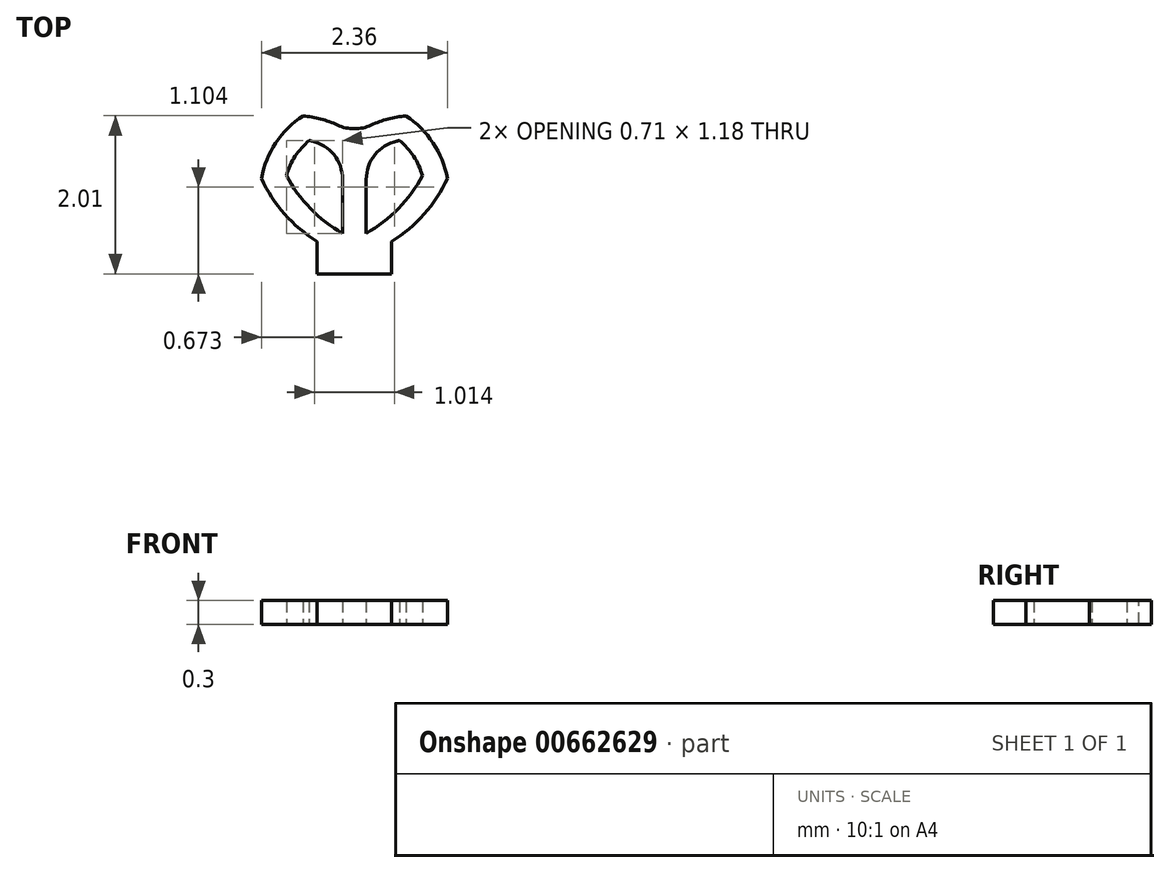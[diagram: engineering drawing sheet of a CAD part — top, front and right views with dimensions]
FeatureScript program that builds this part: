
annotation { "Feature Type Name" : "Feature", "Feature Type Description" : "" }
export const myFeature = defineFeature(function(context is Context, id is Id, definition is map)
    precondition{}
    {
        {
            var Q0;
            Q0=qCreatedBy(makeId("Top.planeOp"),FACE);
            var sketch = newSketch(context, id + "F0", { "sketchPlane" : qUnion([Q0])});
            skArc(sketch, "E0", {"start": v(-0.65, 1) * mm, "mid": v(-1, 0.67) * mm, "end": v(-1.18, 0.21) * mm});
            skLineSegment(sketch, "E1", {"start": v(0, -1) * mm, "end": v(-0.47, -1) * mm});
            skLineSegment(sketch, "E2", {"start": v(-0.47, -1) * mm, "end": v(-0.47, -0.59) * mm});
            skArc(sketch, "E3", {"start": v(0, 0.76) * mm, "mid": v(-0.3, 0.93) * mm, "end": v(-0.65, 1) * mm});
            skArc(sketch, "E4.0", {"start": v(-0.54, 0.69) * mm, "mid": v(-0.56, 0.7) * mm, "end": v(-0.57, 0.7) * mm});
            skArc(sketch, "E5", {"start": v(-0.57, 0.7) * mm, "mid": v(-0.75, 0.5) * mm, "end": v(-0.86, 0.25) * mm});
            skLineSegment(sketch, "E6.0", {"start": v(-0.15, 0.2) * mm, "end": v(-0.15, -0.49) * mm});
            skArc(sketch, "E7", {"start": v(-0.86, 0.25) * mm, "mid": v(-0.56, -0.17) * mm, "end": v(-0.15, -0.49) * mm});
            skArc(sketch, "E8.trimOffspring", {"start": v(-1.18, 0.21) * mm, "mid": v(-0.89, -0.24) * mm, "end": v(-0.47, -0.59) * mm});
            skPoint(sketch, "E9.orphan", {"position": v(-0.47, -0.68) * mm});
            skPoint(sketch, "E10.visualSharp", {"position": v(-0.15, 0.2) * mm});
            skArc(sketch, "E10.filletArc", {"start": v(-0.15, 0.2) * mm, "mid": v(-0.26, 0.51) * mm, "end": v(-0.54, 0.69) * mm});
            skArc(sketch, "E11.MirrorCS", {"start": v(0.54, 0.69) * mm, "mid": v(0.56, 0.7) * mm, "end": v(0.57, 0.7) * mm});
            skLineSegment(sketch, "E12.MirrorCS", {"start": v(0, -1) * mm, "end": v(0.47, -1) * mm});
            skArc(sketch, "E13.MirrorCS", {"start": v(0.65, 1) * mm, "mid": v(1, 0.67) * mm, "end": v(1.18, 0.21) * mm});
            skPoint(sketch, "E14.MirrorP", {"position": v(0.15, 0.2) * mm});
            skArc(sketch, "E15.MirrorCS", {"start": v(0, 0.76) * mm, "mid": v(0.3, 0.93) * mm, "end": v(0.65, 1) * mm});
            skArc(sketch, "E16.MirrorCS", {"start": v(0.57, 0.7) * mm, "mid": v(0.75, 0.5) * mm, "end": v(0.86, 0.25) * mm});
            skArc(sketch, "E17.MirrorCS", {"start": v(1.18, 0.21) * mm, "mid": v(0.89, -0.24) * mm, "end": v(0.47, -0.59) * mm});
            skPoint(sketch, "E18.MirrorP", {"position": v(0.47, -0.68) * mm});
            skArc(sketch, "E19.MirrorCS", {"start": v(0.15, 0.2) * mm, "mid": v(0.26, 0.51) * mm, "end": v(0.54, 0.69) * mm});
            skLineSegment(sketch, "E20.MirrorCS", {"start": v(0.15, 0.2) * mm, "end": v(0.15, -0.49) * mm});
            skLineSegment(sketch, "E21.MirrorCS", {"start": v(0.47, -1) * mm, "end": v(0.47, -0.59) * mm});
            skArc(sketch, "E22.MirrorCS", {"start": v(0.86, 0.25) * mm, "mid": v(0.56, -0.17) * mm, "end": v(0.15, -0.49) * mm});
            skSolve(sketch);
        }
        {
            var Q0;
            Q0=makeQuery(id+"F0.imprint","IMPRINT",FACE,{"disambiguationData":[TD([[makeQuery(id+"F0.imprint","IMPRINT",EDGE,{"derivedFrom":sQuery(id+"F0.wireOp",EDGE,"E0")}),1.0]])]});
            extrude(context, id + "F1", {"entities" : qUnion([Q0]), "depth" : .3 * mm, "offsetDistance" : 25 * mm});
        }
        {
            var Q0;
            Q0=makeQuery(id+"F1.opExtrude","SWEPT_EDGE",EDGE,{"disambiguationData":[OSD([sQuery(id+"F0.wireOp",EDGE,"E3"),sQuery(id+"F0.wireOp",EDGE,"E15.MirrorCS")])]});
            fillet(context, id + "F2", {"entities" : qUnion([Q0]), "radius" : .5 * mm, "tangentPropagation" : true, "allowEdgeOverflow" : false});
        }
    });
